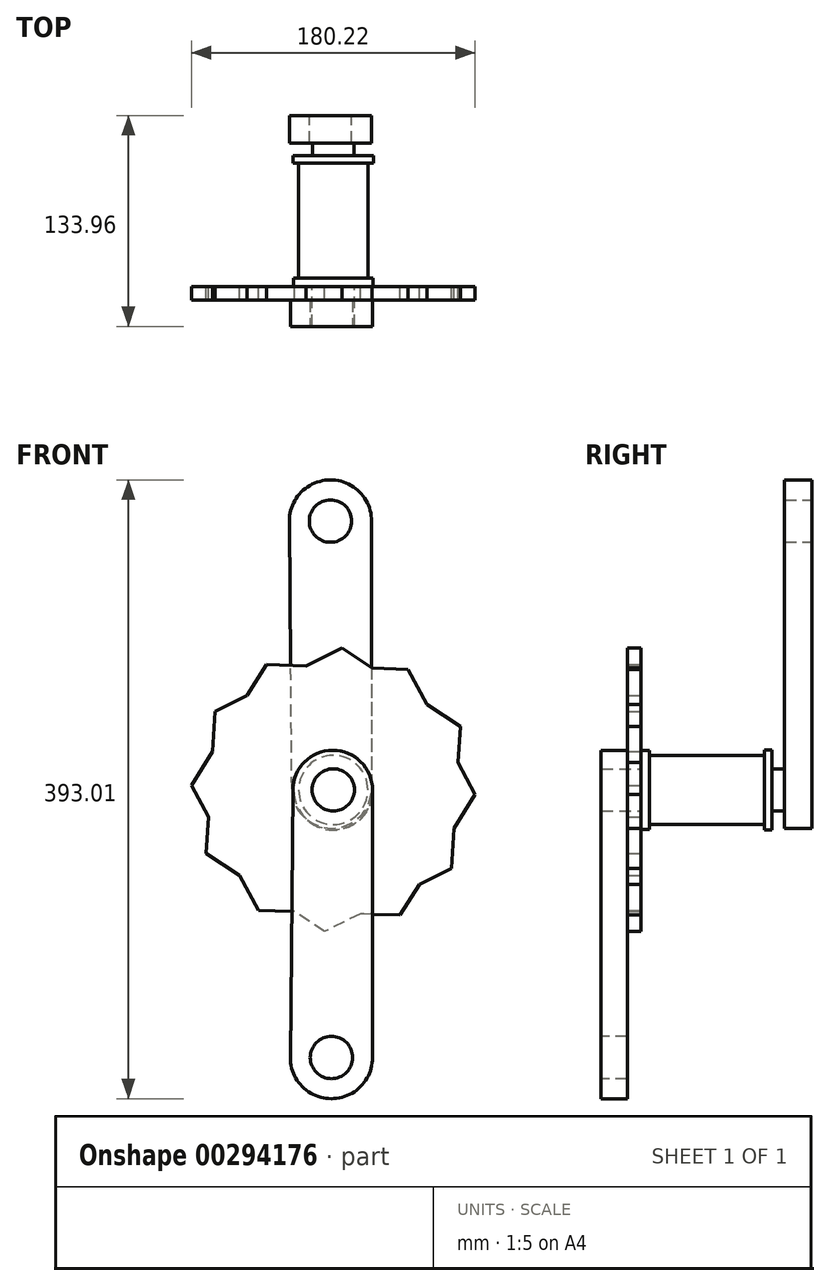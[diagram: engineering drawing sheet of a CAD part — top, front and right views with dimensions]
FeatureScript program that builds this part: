
annotation { "Feature Type Name" : "Feature", "Feature Type Description" : "" }
export const myFeature = defineFeature(function(context is Context, id is Id, definition is map)
    precondition{}
    {
        {
            var Q0;
            Q0=qCreatedBy(makeId("Front.planeOp"),FACE);
            var sketch = newSketch(context, id + "F0", { "sketchPlane" : qUnion([Q0])});
            skCircle(sketch, "E0", {"center": v(0, 0) * mm, "radius": 22 * mm});
            skSolve(sketch);
        }
        {
            var Q0;
            Q0 = qSketchRegion(id + "F0", true);
            extrude(context, id + "F1", {"entities" : qUnion([Q0]), "depth" : 73 * mm});
        }
        {
            var Q0;
            Q0=makeQuery(id+"F1.opExtrude","CAP_FACE",FACE,{"disambiguationData":[OSD([sQuery(id+"F0.wireOp",EDGE,"E0")])],"isStart":false});
            var sketch = newSketch(context, id + "F2", { "sketchPlane" : qUnion([Q0])});
            skCircle(sketch, "E1", {"center": v(0, 0) * mm, "radius": 25.14 * mm});
            skSolve(sketch);
        }
        {
            var Q0;
            Q0 = qSketchRegion(id + "F2", true);
            extrude(context, id + "F3", {"entities" : qUnion([Q0]), "operationType" : NewBodyOperationType.ADD, "depth" : 5.33 * mm});
        }
        {
            var Q0;
            Q0=makeQuery(id+"F1.opExtrude","CAP_FACE",FACE,{"disambiguationData":[OSD([sQuery(id+"F0.wireOp",EDGE,"E0")])],"isStart":true});
            var sketch = newSketch(context, id + "F4", { "sketchPlane" : qUnion([Q0])});
            skCircle(sketch, "E2", {"center": v(0, 0) * mm, "radius": 25.47 * mm});
            skSolve(sketch);
        }
        {
            var Q0;
            Q0 = qSketchRegion(id + "F4", true);
            extrude(context, id + "F5", {"entities" : qUnion([Q0]), "operationType" : NewBodyOperationType.ADD, "depth" : 4.83 * mm});
        }
        {
            var Q0;
            Q0=makeQuery(id+"F5.opExtrude","CAP_FACE",FACE,{"disambiguationData":[OSD([sQuery(id+"F4.wireOp",EDGE,"E2")])],"isStart":false});
            var sketch = newSketch(context, id + "F6", { "sketchPlane" : qUnion([Q0])});
            skCircle(sketch, "E3", {"center": v(0, 0) * mm, "radius": 13.3 * mm});
            skSolve(sketch);
        }
        {
            var Q0;
            Q0=makeQuery(id+"F6.imprint","IMPRINT",FACE,{"disambiguationData":[TD([[makeQuery(id+"F6.imprint","IMPRINT",EDGE,{"derivedFrom":sQuery(id+"F6.wireOp",EDGE,"E3")}),1.0]])]});
            extrude(context, id + "F7", {"entities" : qUnion([Q0]), "depth" : 25.4 * mm});
        }
        {
            var Q0;
            Q0=makeQuery(id+"F3.opExtrude","CAP_FACE",FACE,{"disambiguationData":[OSD([sQuery(id+"F2.wireOp",EDGE,"E1")])],"isStart":false});
            var sketch = newSketch(context, id + "F8", { "sketchPlane" : qUnion([Q0])});
            skCircle(sketch, "E4", {"center": v(0, 0) * mm, "radius": 13.41 * mm});
            skSolve(sketch);
        }
        {
            var Q0;
            Q0 = qSketchRegion(id + "F8", true);
            extrude(context, id + "F9", {"entities" : qUnion([Q0]), "depth" : 25.4 * mm});
        }
        {
            var Q0;
            Q0=makeQuery(id+"F9.opExtrude","CAP_FACE",FACE,{"disambiguationData":[OSD([sQuery(id+"F8.wireOp",EDGE,"E4")])],"isStart":false});
            var sketch = newSketch(context, id + "F10", { "sketchPlane" : qUnion([Q0])});
            skLineSegment(sketch, "E5", {"start": v(0, 0) * mm, "end": v(0, -170) * mm});
            skLineSegment(sketch, "E6", {"start": v(0, 0) * mm, "end": v(24.96, 0) * mm});
            skLineSegment(sketch, "E7", {"start": v(0, 0) * mm, "end": v(-25.72, 0) * mm});
            skArc(sketch, "E8", {"start": v(24.96, 0) * mm, "mid": v(-0.38, 25.1) * mm, "end": v(-25.72, 0) * mm});
            skLineSegment(sketch, "E9", {"start": v(-25.72, 0) * mm, "end": v(-27.3, -169.91) * mm});
            skLineSegment(sketch, "E10", {"start": v(-27.3, -169.91) * mm, "end": v(0, -170) * mm});
            skLineSegment(sketch, "E11", {"start": v(0, -170) * mm, "end": v(24.96, -170) * mm});
            skLineSegment(sketch, "E12", {"start": v(24.96, -170) * mm, "end": v(24.96, 0) * mm});
            skArc(sketch, "E13", {"start": v(-27.3, -169.91) * mm, "mid": v(-1.21, -196.13) * mm, "end": v(24.96, -170) * mm});
            skCircle(sketch, "E14", {"center": v(-1.17, -170) * mm, "radius": 13.46 * mm});
            skSolve(sketch);
        }
        {
            var Q0;
            Q0 = qSketchRegion(id + "F10", true);
            extrude(context, id + "F11", {"entities" : qUnion([Q0]), "oppositeDirection" : true, "depth" : 16.76 * mm});
        }
        {
            var Q0;
            Q0=makeQuery(id+"F7.opExtrude","CAP_FACE",FACE,{"disambiguationData":[OSD([sQuery(id+"F6.wireOp",EDGE,"E3")])],"isStart":false});
            var sketch = newSketch(context, id + "F12", { "sketchPlane" : qUnion([Q0])});
            skLineSegment(sketch, "E15", {"start": v(0.6, 0.75) * mm, "end": v(0.6, 170.75) * mm});
            skLineSegment(sketch, "E16", {"start": v(0.6, 0.75) * mm, "end": v(-24.35, 0.75) * mm});
            skLineSegment(sketch, "E17", {"start": v(0.6, 0.75) * mm, "end": v(26.32, 0.75) * mm});
            skArc(sketch, "E18", {"start": v(-24.35, 0.75) * mm, "mid": v(0.98, -24.36) * mm, "end": v(26.32, 0.75) * mm});
            skLineSegment(sketch, "E19", {"start": v(26.32, 0.75) * mm, "end": v(27.9, 170.66) * mm});
            skLineSegment(sketch, "E20", {"start": v(27.9, 170.66) * mm, "end": v(0.6, 170.75) * mm});
            skLineSegment(sketch, "E21", {"start": v(0.6, 170.75) * mm, "end": v(-24.35, 170.75) * mm});
            skLineSegment(sketch, "E22", {"start": v(-24.35, 170.75) * mm, "end": v(-24.35, 0.75) * mm});
            skArc(sketch, "E23", {"start": v(27.9, 170.66) * mm, "mid": v(1.82, 196.88) * mm, "end": v(-24.35, 170.75) * mm});
            skCircle(sketch, "E24", {"center": v(1.78, 170.75) * mm, "radius": 13.46 * mm});
            skSolve(sketch);
        }
        {
            var Q0;
            Q0 = qSketchRegion(id + "F12", true);
            extrude(context, id + "F13", {"entities" : qUnion([Q0]), "operationType" : NewBodyOperationType.ADD, "oppositeDirection" : true, "depth" : 17.53 * mm});
        }
        {
            var Q0;
            Q0=makeQuery(id+"F3.opExtrude","CAP_FACE",FACE,{"disambiguationData":[OSD([sQuery(id+"F2.wireOp",EDGE,"E1")])],"isStart":false});
            var sketch = newSketch(context, id + "F14", { "sketchPlane" : qUnion([Q0])});
            skCircle(sketch, "E25.cCircle", {"center": v(0, 0) * mm, "radius": 78.08 * mm, "construction": true});
            skLineSegment(sketch, "E25.0", {"start": v(47.6, 76.57) * mm, "end": v(90.11, -2.95) * mm});
            skLineSegment(sketch, "E25.1", {"start": v(90.11, -2.95) * mm, "end": v(42.5, -79.51) * mm});
            skLineSegment(sketch, "E25.2", {"start": v(42.5, -79.51) * mm, "end": v(-47.6, -76.57) * mm});
            skLineSegment(sketch, "E25.3", {"start": v(-47.6, -76.57) * mm, "end": v(-90.11, 2.95) * mm});
            skLineSegment(sketch, "E25.4", {"start": v(-90.11, 2.95) * mm, "end": v(-42.5, 79.51) * mm});
            skLineSegment(sketch, "E25.5", {"start": v(-42.5, 79.51) * mm, "end": v(47.6, 76.57) * mm});
            skPoint(sketch, "E25.0.midPoint", {"position": v(68.86, 36.8) * mm});
            skLineSegment(sketch, "E26.0", {"start": v(5.53, 89.99) * mm, "end": v(80.7, 40.2) * mm});
            skLineSegment(sketch, "E26.1", {"start": v(80.7, 40.2) * mm, "end": v(75.17, -49.78) * mm});
            skLineSegment(sketch, "E26.2", {"start": v(75.17, -49.78) * mm, "end": v(-5.53, -89.99) * mm});
            skLineSegment(sketch, "E26.3", {"start": v(-5.53, -89.99) * mm, "end": v(-80.7, -40.2) * mm});
            skLineSegment(sketch, "E26.4", {"start": v(-80.7, -40.2) * mm, "end": v(-75.17, 49.78) * mm});
            skLineSegment(sketch, "E26.5", {"start": v(-75.17, 49.78) * mm, "end": v(5.53, 89.99) * mm});
            skPoint(sketch, "E26.0.midPoint", {"position": v(43.11, 65.1) * mm});
            skSolve(sketch);
        }
        {
            var Q0;
            Q0 = qSketchRegion(id + "F14", true);
            extrude(context, id + "F15", {"entities" : qUnion([Q0]), "depth" : 8.64 * mm});
        }
    });
